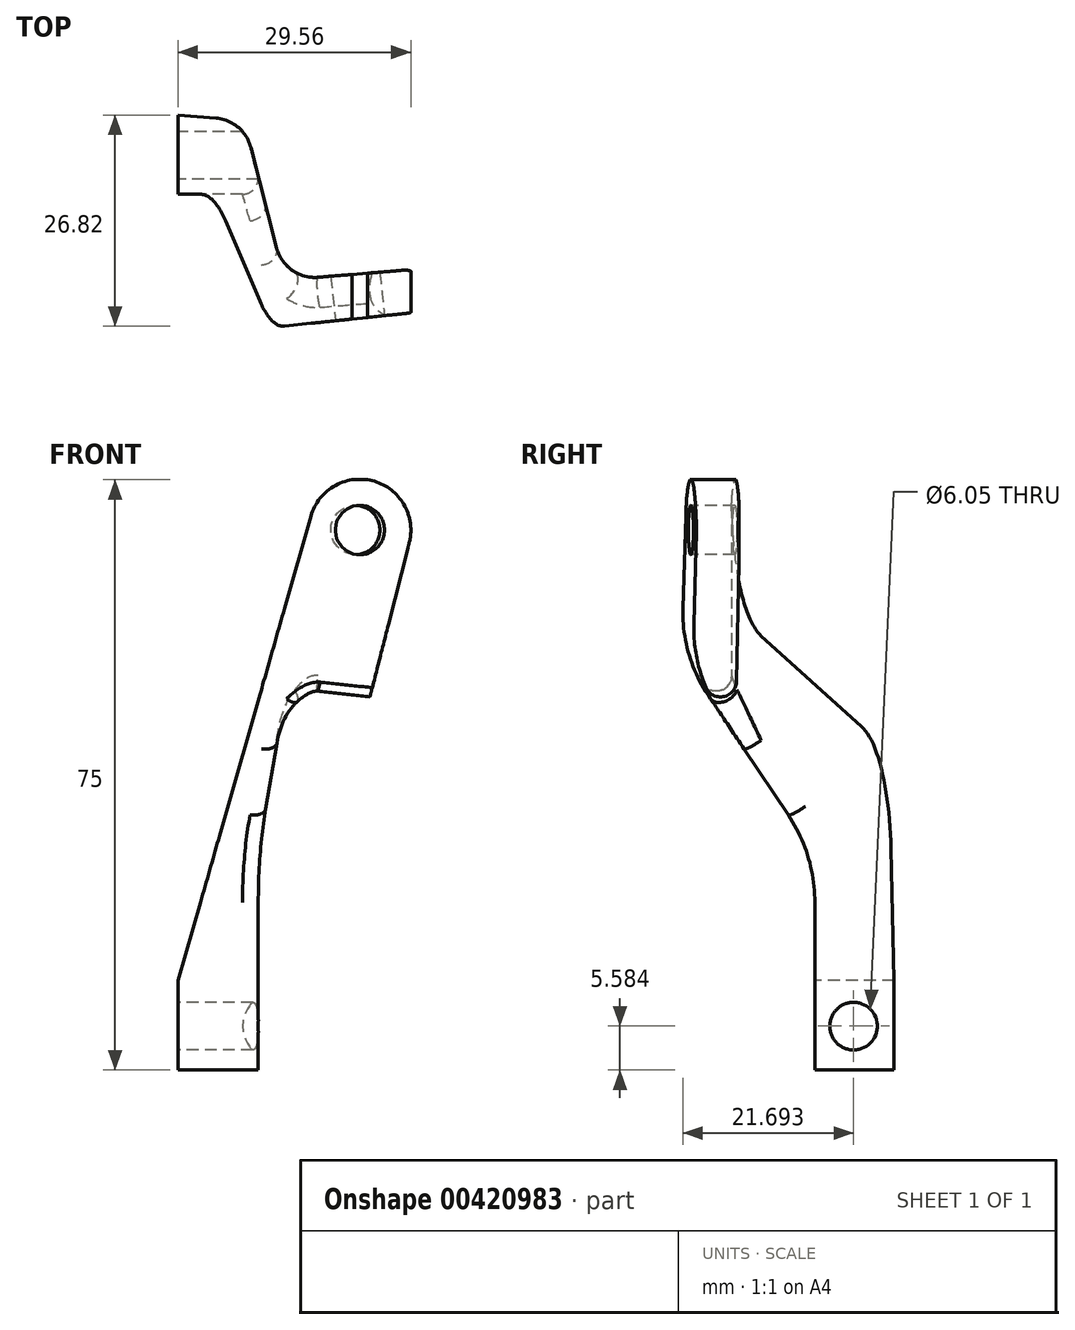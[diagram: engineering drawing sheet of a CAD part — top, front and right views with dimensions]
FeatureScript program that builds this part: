
annotation { "Feature Type Name" : "Feature", "Feature Type Description" : "" }
export const myFeature = defineFeature(function(context is Context, id is Id, definition is map)
    precondition{}
    {
        {
            var Q0;
            Q0=qCreatedBy(makeId("Top.planeOp"),FACE);
            var sketch = newSketch(context, id + "F0", { "sketchPlane" : qUnion([Q0])});
            skLineSegment(sketch, "E0", {"start": v(0, 0) * mm, "end": v(0, 10.05) * mm});
            skLineSegment(sketch, "E1", {"start": v(0, 10.05) * mm, "end": v(4.8, 9.67) * mm});
            skLineSegment(sketch, "E2", {"start": v(9.24, 5.94) * mm, "end": v(12.52, -6.82) * mm});
            skLineSegment(sketch, "E3", {"start": v(17.78, -10.56) * mm, "end": v(28.68, -9.65) * mm});
            skLineSegment(sketch, "E4", {"start": v(30.84, -11.48) * mm, "end": v(30.97, -12.96) * mm});
            skLineSegment(sketch, "E5", {"start": v(29.18, -15.12) * mm, "end": v(9.31, -17.2) * mm});
            skLineSegment(sketch, "E6", {"start": v(4, -13.63) * mm, "end": v(0, 0) * mm});
            skPoint(sketch, "E7.visualSharp", {"position": v(13.58, -10.9) * mm});
            skArc(sketch, "E7.filletArc", {"start": v(12.52, -6.82) * mm, "mid": v(14.47, -9.65) * mm, "end": v(17.78, -10.56) * mm});
            skPoint(sketch, "E8.visualSharp", {"position": v(8.35, 9.4) * mm});
            skArc(sketch, "E8.filletArc", {"start": v(9.24, 5.94) * mm, "mid": v(7.62, 8.52) * mm, "end": v(4.8, 9.67) * mm});
            skPoint(sketch, "E9.visualSharp", {"position": v(5.17, -17.63) * mm});
            skArc(sketch, "E9.filletArc", {"start": v(4, -13.63) * mm, "mid": v(6, -16.38) * mm, "end": v(9.31, -17.2) * mm});
            skPoint(sketch, "E10.visualSharp", {"position": v(31.13, -14.91) * mm});
            skArc(sketch, "E10.filletArc", {"start": v(29.18, -15.12) * mm, "mid": v(30.51, -14.4) * mm, "end": v(30.97, -12.96) * mm});
            skPoint(sketch, "E11.visualSharp", {"position": v(30.68, -9.49) * mm});
            skArc(sketch, "E11.filletArc", {"start": v(30.84, -11.48) * mm, "mid": v(30.14, -10.12) * mm, "end": v(28.68, -9.65) * mm});
            skSolve(sketch);
        }
        {
            var Q0;
            Q0 = qSketchRegion(id + "F0", true);
            extrude(context, id + "F1", {"entities" : qUnion([Q0]), "depth" : 75 * mm});
        }
        {
            var Q0;
            Q0=qCreatedBy(makeId("Front.planeOp"),FACE);
            var sketch = newSketch(context, id + "F2", { "sketchPlane" : qUnion([Q0])});
            skArc(sketch, "E12", {"start": v(29.36, 67) * mm, "mid": v(24.78, 74.85) * mm, "end": v(16.88, 70.38) * mm});
            skLineSegment(sketch, "E13", {"start": v(0, 0) * mm, "end": v(0, 11.36) * mm});
            skLineSegment(sketch, "E14", {"start": v(0, 11.36) * mm, "end": v(16.88, 70.38) * mm});
            skLineSegment(sketch, "E15", {"start": v(0, 0) * mm, "end": v(12.3, 0) * mm});
            skLineSegment(sketch, "E16", {"start": v(12.3, 0) * mm, "end": v(29.36, 67) * mm});
            skLineSegment(sketch, "E17", {"start": v(12.3, 0) * mm, "end": v(38.13, 0) * mm});
            skLineSegment(sketch, "E18", {"start": v(38.13, 0) * mm, "end": v(39.9, 75.09) * mm});
            skLineSegment(sketch, "E19", {"start": v(39.9, 75.09) * mm, "end": v(23.12, 75.07) * mm});
            skLineSegment(sketch, "E20", {"start": v(23.12, 75.07) * mm, "end": v(0, 75.07) * mm});
            skLineSegment(sketch, "E21", {"start": v(0, 75.07) * mm, "end": v(0, 11.36) * mm});
            skLineSegment(sketch, "E22", {"start": v(0, 11.36) * mm, "end": v(0, 75.07) * mm});
            skSolve(sketch);
        }
        {
            var Q0;
            {var subQ0=sQuery(id+"F2.wireOp",EDGE,"E16");Q0=makeQuery(id+"F2.imprint","IMPRINT",FACE,{"disambiguationData":[TD([[makeQuery(id+"F2.imprint","IMPRINT",EDGE,{"derivedFrom":subQ0}),-1.0]])]});}
            var Q1;
            {var subQ0=sQuery(id+"F2.wireOp",EDGE,"E14");Q1=makeQuery(id+"F2.imprint","IMPRINT",FACE,{"disambiguationData":[TD([[makeQuery(id+"F2.imprint","IMPRINT",EDGE,{"derivedFrom":subQ0}),1.0]])]});}
            extrude(context, id + "F3", {"entities" : qUnion([Q0, Q1]), "operationType" : NewBodyOperationType.REMOVE, "endBound" : BoundingType.SYMMETRIC, "oppositeDirection" : true, "depth" : 40 * mm});
        }
        {
            var Q0;
            Q0=qCreatedBy(makeId("Right.planeOp"),FACE);
            var sketch = newSketch(context, id + "F4", { "sketchPlane" : qUnion([Q0])});
            skLineSegment(sketch, "E23", {"start": v(0, 0) * mm, "end": v(0, 27.36) * mm});
            skLineSegment(sketch, "E24", {"start": v(0, 27.36) * mm, "end": v(-32.03, 75.26) * mm});
            skLineSegment(sketch, "E25", {"start": v(-32.03, 75.26) * mm, "end": v(-32.03, 0) * mm});
            skLineSegment(sketch, "E26", {"start": v(-32.03, 0) * mm, "end": v(0, 0) * mm});
            skSolve(sketch);
        }
        {
            var Q0;
            Q0 = qSketchRegion(id + "F4", true);
            extrude(context, id + "F5", {"entities" : qUnion([Q0]), "operationType" : NewBodyOperationType.REMOVE, "endBound" : BoundingType.SYMMETRIC, "depth" : 60 * mm});
        }
        {
            var Q0;
            Q0=makeQuery(id+"F5.boolean.opBoolean","INTERSECT",EDGE,{"derivedFrom":[makeQuery(id+"F1.opExtrude","SWEPT_FACE",FACE,{"disambiguationData":[OSD([sQuery(id+"F0.wireOp",EDGE,"E5")])]}),makeQuery(id+"F5.opExtrude","SWEPT_FACE",FACE,{"disambiguationData":[OSD([sQuery(id+"F4.wireOp",EDGE,"E24")])]})]});
            var Q1;
            Q1=makeQuery(id+"F5.boolean.opBoolean","COPY",EDGE,{"derivedFrom":makeQuery(id+"F5.opExtrude","SWEPT_EDGE",EDGE,{"disambiguationData":[OSD([sQuery(id+"F4.wireOp",EDGE,"E23"),sQuery(id+"F4.wireOp",EDGE,"E24")])]})});
            fillet(context, id + "F6", {"entities" : qUnion([Q0, Q1]), "radius" : 20 * mm, "tangentPropagation" : true, "allowEdgeOverflow" : false});
        }
        {
            var Q0;
            Q0=makeQuery(id+"F5.boolean.opBoolean","INTERSECT",EDGE,{"derivedFrom":[makeQuery(id+"F1.opExtrude","SWEPT_FACE",FACE,{"disambiguationData":[OSD([sQuery(id+"F0.wireOp",EDGE,"E7.filletArc")])]}),makeQuery(id+"F5.opExtrude","SWEPT_FACE",FACE,{"disambiguationData":[OSD([sQuery(id+"F4.wireOp",EDGE,"E24")])]})]});
            fillet(context, id + "F7", {"entities" : qUnion([Q0]), "radius" : 2 * mm, "tangentPropagation" : true, "allowEdgeOverflow" : false});
        }
        {
            var Q0;
            Q0=makeQuery(id+"F1.opExtrude","SWEPT_FACE",FACE,{"disambiguationData":[OSD([sQuery(id+"F0.wireOp",EDGE,"E0")])]});
            var sketch = newSketch(context, id + "F8", { "sketchPlane" : qUnion([Q0])});
            skCircle(sketch, "E27", {"center": v(-4.92, 5.58) * mm, "radius": 3.03 * mm});
            skSolve(sketch);
        }
        {
            var Q0;
            Q0 = qSketchRegion(id + "F8", true);
            extrude(context, id + "F9", {"entities" : qUnion([Q0]), "operationType" : NewBodyOperationType.REMOVE, "oppositeDirection" : true, "depth" : 25 * mm});
        }
        {
            var Q0;
            Q0=makeQuery(id+"F1.opExtrude","SWEPT_FACE",FACE,{"disambiguationData":[OSD([sQuery(id+"F0.wireOp",EDGE,"E5")])]});
            var sketch = newSketch(context, id + "F10", { "sketchPlane" : qUnion([Q0])});
            skCircle(sketch, "E28", {"center": v(21.33, 68.6) * mm, "radius": 3.14 * mm});
            skSolve(sketch);
        }
        {
            var Q0;
            Q0 = qSketchRegion(id + "F10", true);
            extrude(context, id + "F11", {"entities" : qUnion([Q0]), "operationType" : NewBodyOperationType.REMOVE, "oppositeDirection" : true, "depth" : 25 * mm});
        }
    });
